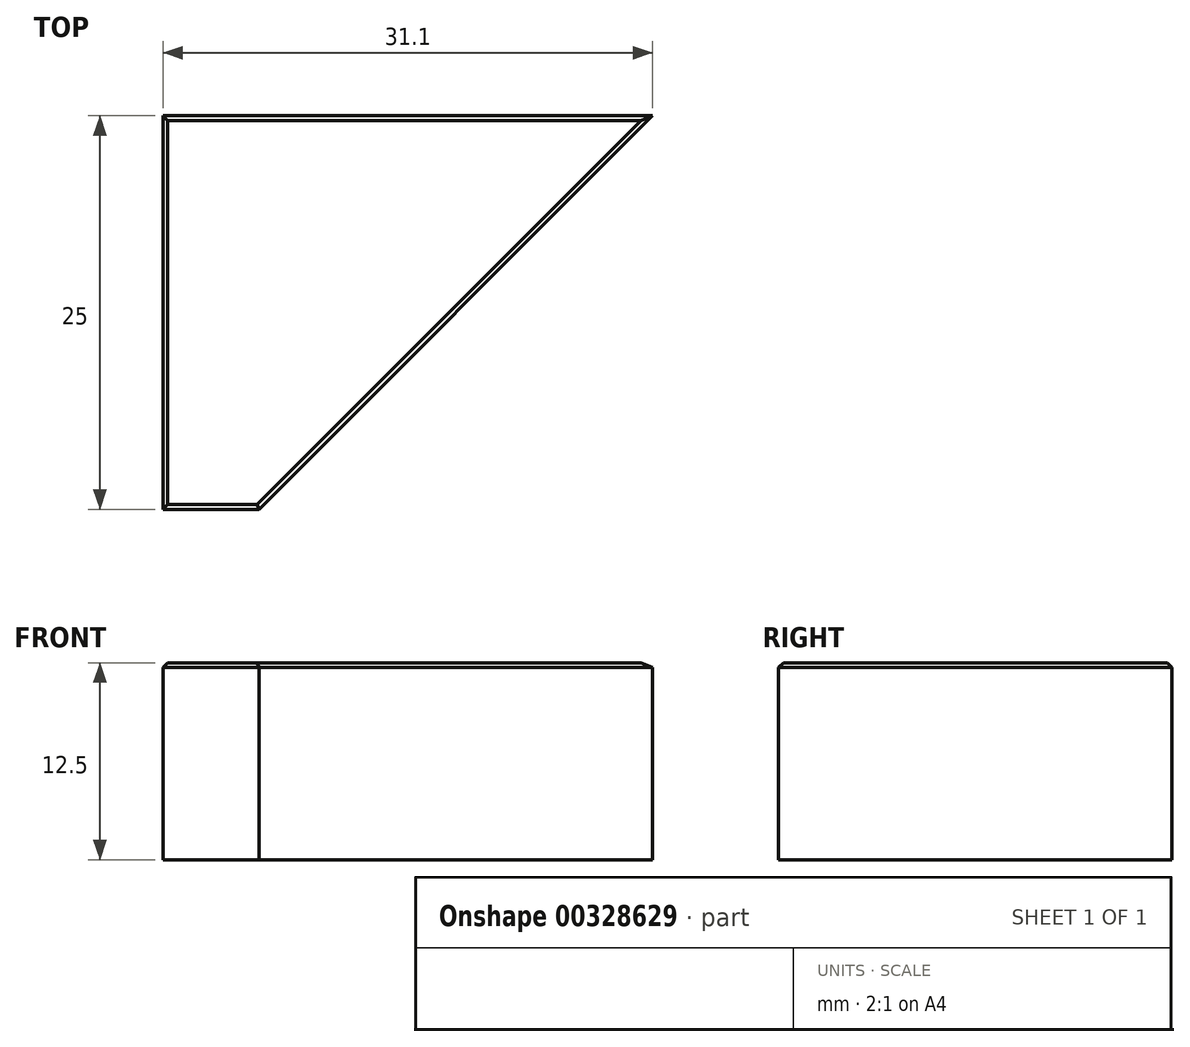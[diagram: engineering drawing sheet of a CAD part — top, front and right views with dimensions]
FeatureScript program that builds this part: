
annotation { "Feature Type Name" : "Feature", "Feature Type Description" : "" }
export const myFeature = defineFeature(function(context is Context, id is Id, definition is map)
    precondition{}
    {
        {
            var Q0;
            Q0=qCreatedBy(makeId("Top.planeOp"),FACE);
            var sketch = newSketch(context, id + "F0", { "sketchPlane" : qUnion([Q0])});
            skLineSegment(sketch, "E0.bottom", {"start": v(31.1, 0) * mm, "end": v(0, 0) * mm});
            skLineSegment(sketch, "E0.top", {"start": v(6.1, -25) * mm, "end": v(0, -25) * mm});
            skLineSegment(sketch, "E0.right", {"start": v(0, 0) * mm, "end": v(0, -25) * mm});
            skLineSegment(sketch, "E1", {"start": v(6.1, -25) * mm, "end": v(31.1, 0) * mm});
            skSolve(sketch);
        }
        {
            var Q0;
            Q0=qSketchRegion(id+"F0",true);
            extrude(context, id + "F1", {"entities" : qUnion([Q0]), "oppositeDirection" : true, "depth" : 12.5 * mm});
        }
        {
            var Q0;
            Q0=makeQuery(id+"F1.opExtrude","CAP_FACE",FACE,{"disambiguationData":[OSD([sQuery(id+"F0.wireOp",EDGE,"E0.bottom"),sQuery(id+"F0.wireOp",EDGE,"E0.top"),sQuery(id+"F0.wireOp",EDGE,"E0.left"),sQuery(id+"F0.wireOp",EDGE,"E0.right")])],"isStart":true});
            chamfer(context, id + "F2", {"entities" : qUnion([Q0]), "width" : .3 * mm, "tangentPropagation" : true});
        }
    });
